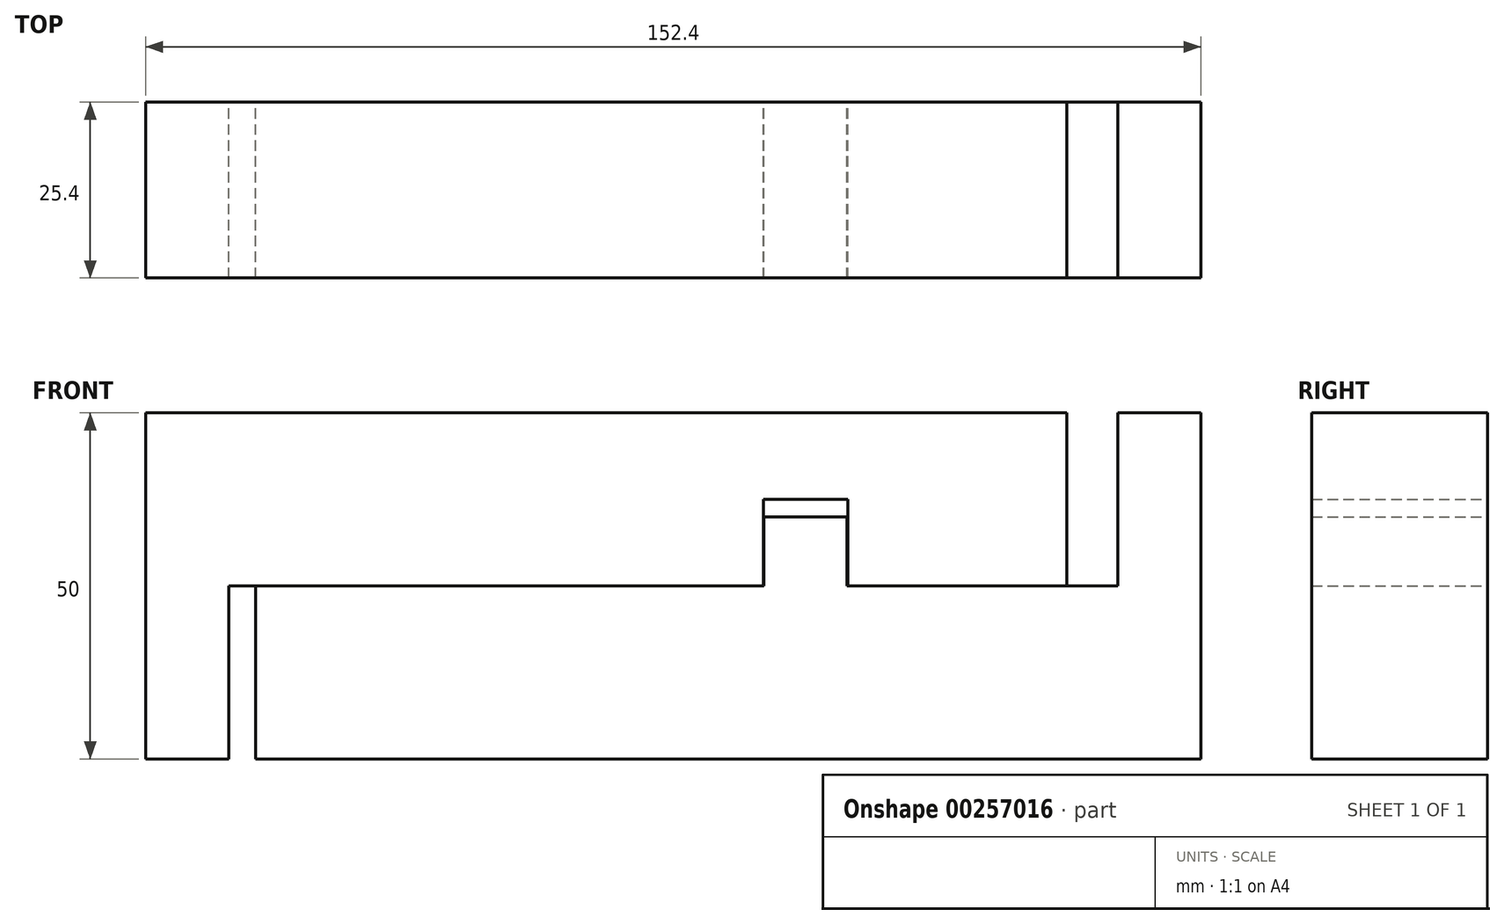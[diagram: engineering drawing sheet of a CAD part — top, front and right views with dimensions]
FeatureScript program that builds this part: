
annotation { "Feature Type Name" : "Feature", "Feature Type Description" : "" }
export const myFeature = defineFeature(function(context is Context, id is Id, definition is map)
    precondition{}
    {
        {
            var Q0;
            Q0=qCreatedBy(makeId("Front.planeOp"),FACE);
            var sketch = newSketch(context, id + "F0", { "sketchPlane" : qUnion([Q0])});
            skLineSegment(sketch, "E0", {"start": v(0, 0) * mm, "end": v(0, 50) * mm});
            skLineSegment(sketch, "E1", {"start": v(0, 50) * mm, "end": v(133, 50) * mm});
            skLineSegment(sketch, "E2", {"start": v(133, 50) * mm, "end": v(133, 25) * mm});
            skLineSegment(sketch, "E3", {"start": v(133, 25) * mm, "end": v(101.38, 25) * mm});
            skLineSegment(sketch, "E4", {"start": v(101.38, 25) * mm, "end": v(101.38, 37.5) * mm});
            skLineSegment(sketch, "E5", {"start": v(101.38, 37.5) * mm, "end": v(89.22, 37.5) * mm});
            skLineSegment(sketch, "E6", {"start": v(89.22, 37.5) * mm, "end": v(89.22, 25) * mm});
            skLineSegment(sketch, "E7", {"start": v(89.22, 25) * mm, "end": v(12, 25) * mm});
            skLineSegment(sketch, "E8", {"start": v(12, 25) * mm, "end": v(12, 0) * mm});
            skLineSegment(sketch, "E9", {"start": v(12, 0) * mm, "end": v(0, 0) * mm});
            skLineSegment(sketch, "E10", {"start": v(95.3, 37.5) * mm, "end": v(95.3, 14.37) * mm, "construction": true});
            skSolve(sketch);
        }
        {
            var Q0;
            Q0 = qSketchRegion(id + "F0", true);
            extrude(context, id + "F1", {"entities" : qUnion([Q0]), "depth" : 25.4 * mm});
        }
        {
            var Q0;
            Q0=qCreatedBy(makeId("Front.planeOp"),FACE);
            var sketch = newSketch(context, id + "F2", { "sketchPlane" : qUnion([Q0])});
            skLineSegment(sketch, "E11", {"start": v(15.9, 0) * mm, "end": v(15.9, 25) * mm});
            skLineSegment(sketch, "E12", {"start": v(15.9, 25) * mm, "end": v(89.3, 25) * mm});
            skLineSegment(sketch, "E13", {"start": v(89.3, 25) * mm, "end": v(89.3, 35) * mm});
            skLineSegment(sketch, "E14", {"start": v(89.3, 35) * mm, "end": v(101.3, 35) * mm});
            skLineSegment(sketch, "E15", {"start": v(101.3, 35) * mm, "end": v(101.3, 25) * mm});
            skLineSegment(sketch, "E16", {"start": v(101.3, 25) * mm, "end": v(140.4, 25) * mm});
            skLineSegment(sketch, "E17", {"start": v(140.4, 25) * mm, "end": v(140.4, 50) * mm});
            skLineSegment(sketch, "E18", {"start": v(140.4, 50) * mm, "end": v(152.4, 50) * mm});
            skLineSegment(sketch, "E19", {"start": v(152.4, 50) * mm, "end": v(152.4, 0) * mm});
            skLineSegment(sketch, "E20", {"start": v(152.4, 0) * mm, "end": v(15.9, 0) * mm});
            skLineSegment(sketch, "E21", {"start": v(95.3, 35) * mm, "end": v(95.3, 37.5) * mm, "construction": true});
            skSolve(sketch);
        }
        {
            var Q0;
            Q0 = qSketchRegion(id + "F2", true);
            extrude(context, id + "F3", {"entities" : qUnion([Q0]), "depth" : 25.4 * mm});
        }
    });
